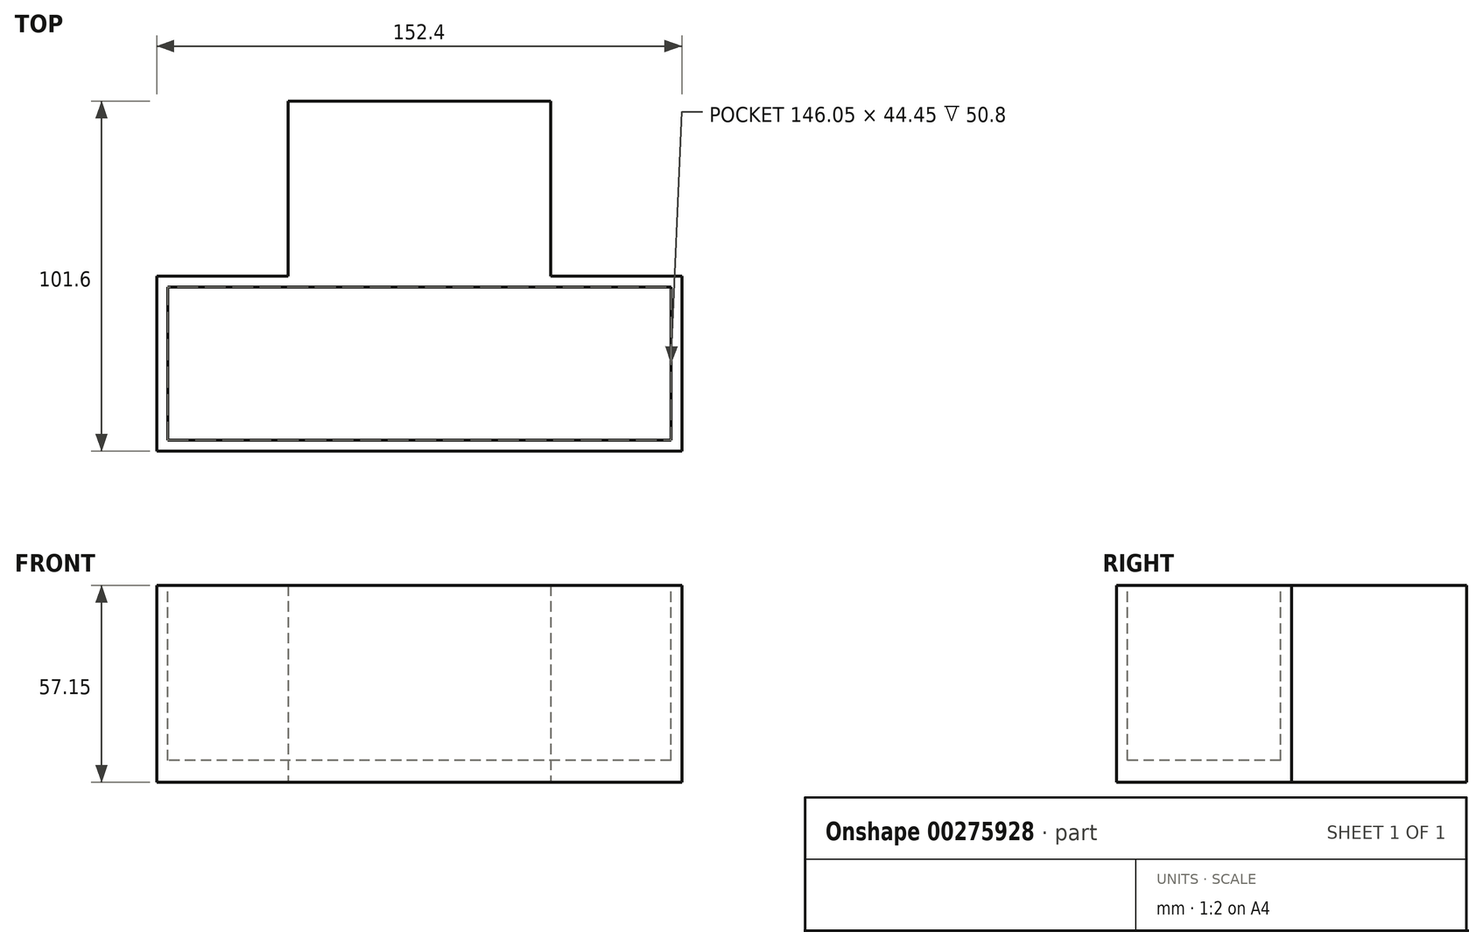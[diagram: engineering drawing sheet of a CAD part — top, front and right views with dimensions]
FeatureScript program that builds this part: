
annotation { "Feature Type Name" : "Feature", "Feature Type Description" : "" }
export const myFeature = defineFeature(function(context is Context, id is Id, definition is map)
    precondition{}
    {
        {
            var Q0;
            Q0=qCreatedBy(makeId("Top.planeOp"),FACE);
            var sketch = newSketch(context, id + "F0", { "sketchPlane" : qUnion([Q0])});
            skLineSegment(sketch, "E0.bottom", {"start": v(76.2, 25.4) * mm, "end": v(-76.2, 25.4) * mm});
            skLineSegment(sketch, "E0.top", {"start": v(76.2, -25.4) * mm, "end": v(-76.2, -25.4) * mm});
            skLineSegment(sketch, "E0.left", {"start": v(76.2, 25.4) * mm, "end": v(76.2, -25.4) * mm});
            skLineSegment(sketch, "E0.right", {"start": v(-76.2, 25.4) * mm, "end": v(-76.2, -25.4) * mm});
            skPoint(sketch, "E0.middle", {"position": v(0, 0) * mm});
            skLineSegment(sketch, "E1", {"start": v(0, 0) * mm, "end": v(0, 50.8) * mm});
            skLineSegment(sketch, "E2.bottom", {"start": v(38.1, 25.4) * mm, "end": v(-38.1, 25.4) * mm});
            skLineSegment(sketch, "E2.top", {"start": v(38.1, 76.2) * mm, "end": v(-38.1, 76.2) * mm});
            skLineSegment(sketch, "E2.left", {"start": v(38.1, 25.4) * mm, "end": v(38.1, 76.2) * mm});
            skLineSegment(sketch, "E2.right", {"start": v(-38.1, 25.4) * mm, "end": v(-38.1, 76.2) * mm});
            skPoint(sketch, "E2.middle", {"position": v(0, 50.8) * mm});
            skPoint(sketch, "E3", {"position": v(-38.1, 50.8) * mm});
            skPoint(sketch, "E4", {"position": v(38.1, 50.8) * mm});
            skLineSegment(sketch, "E5", {"start": v(-38.1, 50.8) * mm, "end": v(0, 50.8) * mm});
            skLineSegment(sketch, "E6", {"start": v(0, 50.8) * mm, "end": v(38.1, 50.8) * mm});
            skPoint(sketch, "E7", {"position": v(-104.2, 50.8) * mm});
            skPoint(sketch, "E8", {"position": v(19.05, 50.8) * mm});
            skPoint(sketch, "E9", {"position": v(-19.05, 50.8) * mm});
            skSolve(sketch);
        }
        {
            var Q0;
            Q0=qSketchRegion(id+"F0",true);
            extrude(context, id + "F1", {"entities" : qUnion([Q0]), "depth" : 57.15 * mm});
        }
        {
            var Q0;
            Q0=makeQuery(id+"F1.opExtrude","CAP_FACE",FACE,{"disambiguationData":[OSD([sQuery(id+"F0.wireOp",EDGE,"E0.bottom"),sQuery(id+"F0.wireOp",EDGE,"E0.top"),sQuery(id+"F0.wireOp",EDGE,"E0.left"),sQuery(id+"F0.wireOp",EDGE,"E0.right"),sQuery(id+"F0.wireOp",EDGE,"E2.top"),sQuery(id+"F0.wireOp",EDGE,"E2.left"),sQuery(id+"F0.wireOp",EDGE,"E2.right")])],"isStart":false});
            var sketch = newSketch(context, id + "F2", { "sketchPlane" : qUnion([Q0])});
            skLineSegment(sketch, "E10.bottom", {"start": v(73.03, 22.23) * mm, "end": v(-73.03, 22.23) * mm});
            skLineSegment(sketch, "E10.top", {"start": v(73.03, -22.23) * mm, "end": v(-73.03, -22.23) * mm});
            skLineSegment(sketch, "E10.left", {"start": v(73.03, 22.23) * mm, "end": v(73.03, -22.23) * mm});
            skLineSegment(sketch, "E10.right", {"start": v(-73.03, 22.23) * mm, "end": v(-73.03, -22.23) * mm});
            skPoint(sketch, "E10.middle", {"position": v(0, 0) * mm});
            skSolve(sketch);
        }
        {
            var Q0;
            Q0=qSketchRegion(id+"F2",true);
            extrude(context, id + "F3", {"entities" : qUnion([Q0]), "operationType" : NewBodyOperationType.REMOVE, "oppositeDirection" : true, "depth" : 50.8 * mm});
        }
    });
